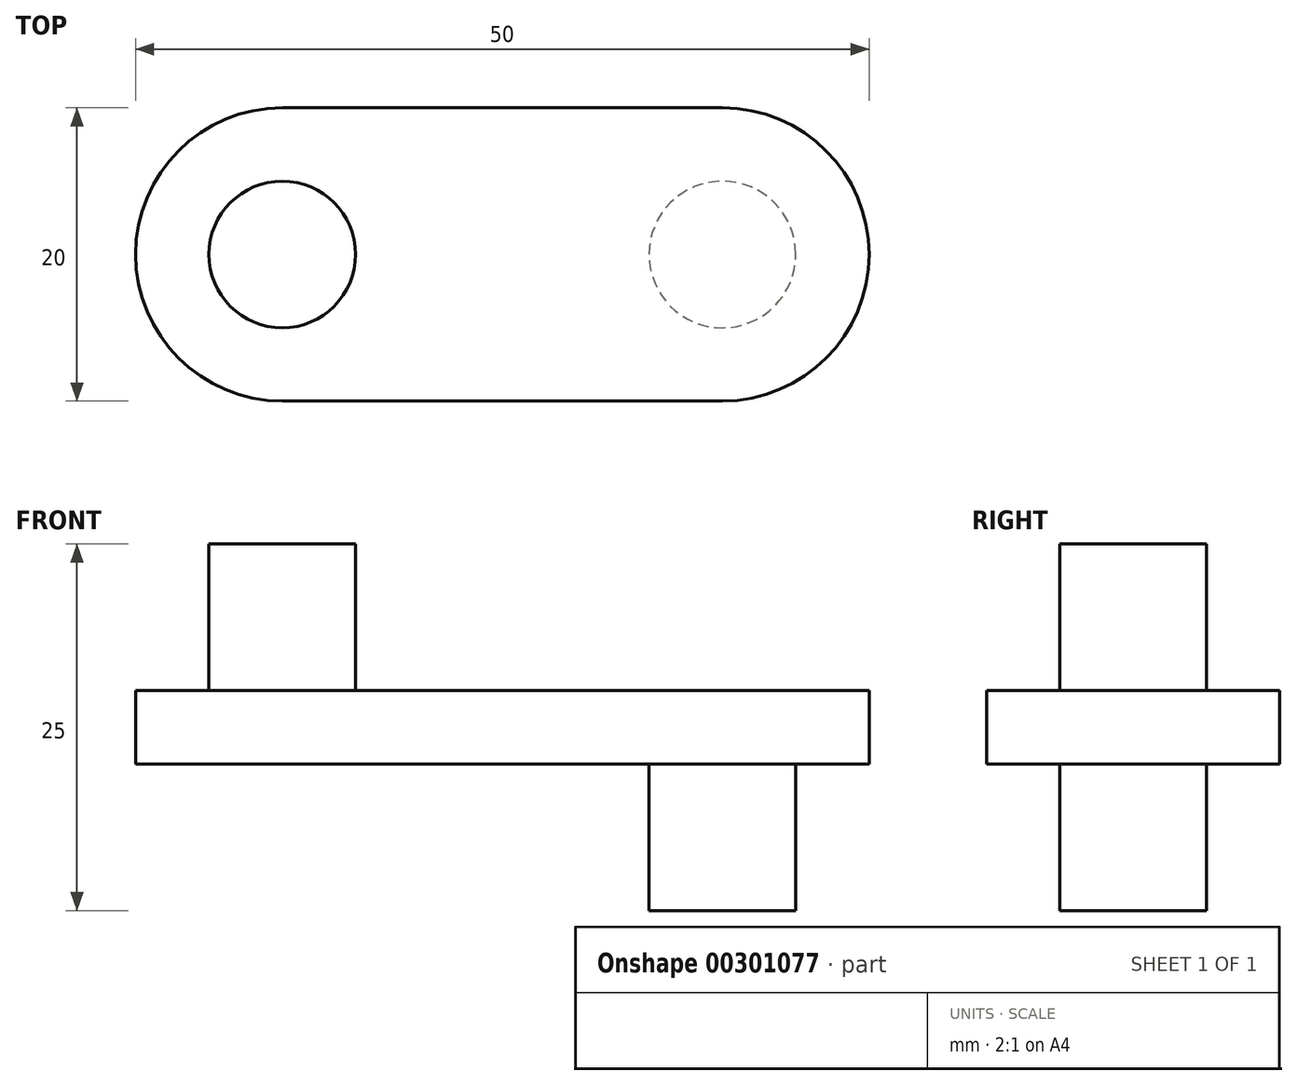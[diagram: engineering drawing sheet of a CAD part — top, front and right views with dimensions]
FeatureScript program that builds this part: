
annotation { "Feature Type Name" : "Feature", "Feature Type Description" : "" }
export const myFeature = defineFeature(function(context is Context, id is Id, definition is map)
    precondition{}
    {
        {
            var Q0;
            Q0=qCreatedBy(makeId("Top.planeOp"),FACE);
            var sketch = newSketch(context, id + "F0", { "sketchPlane" : qUnion([Q0])});
            skLineSegment(sketch, "E0", {"start": v(0, 0) * mm, "end": v(30, 0) * mm});
            skLineSegment(sketch, "E1", {"start": v(0, 20) * mm, "end": v(30, 20) * mm});
            skArc(sketch, "E2", {"start": v(0, 20) * mm, "mid": v(-10, 10) * mm, "end": v(0, 0) * mm});
            skArc(sketch, "E3", {"start": v(30, 0) * mm, "mid": v(40, 10) * mm, "end": v(30, 20) * mm});
            skSolve(sketch);
        }
        {
            var Q0;
            Q0 = qSketchRegion(id + "F0", true);
            extrude(context, id + "F1", {"entities" : qUnion([Q0]), "depth" : 5 * mm});
        }
        {
            var Q0;
            Q0=makeQuery(id+"F1.opExtrude","CAP_FACE",FACE,{"disambiguationData":[OSD([sQuery(id+"F0.wireOp",EDGE,"E0"),sQuery(id+"F0.wireOp",EDGE,"E1"),sQuery(id+"F0.wireOp",EDGE,"E2"),sQuery(id+"F0.wireOp",EDGE,"E3")])],"isStart":false});
            var sketch = newSketch(context, id + "F2", { "sketchPlane" : qUnion([Q0])});
            skCircle(sketch, "E4", {"center": v(0, 10) * mm, "radius": 5 * mm});
            skSolve(sketch);
        }
        {
            var Q0;
            Q0 = qSketchRegion(id + "F2", true);
            extrude(context, id + "F3", {"entities" : qUnion([Q0]), "operationType" : NewBodyOperationType.ADD, "depth" : 10 * mm});
        }
        {
            var Q0;
            Q0=makeQuery(id+"F1.opExtrude","CAP_FACE",FACE,{"disambiguationData":[OSD([sQuery(id+"F0.wireOp",EDGE,"E0"),sQuery(id+"F0.wireOp",EDGE,"E1"),sQuery(id+"F0.wireOp",EDGE,"E2"),sQuery(id+"F0.wireOp",EDGE,"E3")])],"isStart":true});
            var sketch = newSketch(context, id + "F4", { "sketchPlane" : qUnion([Q0])});
            skCircle(sketch, "E5", {"center": v(30, -10) * mm, "radius": 5 * mm});
            skSolve(sketch);
        }
        {
            var Q0;
            Q0 = qSketchRegion(id + "F4", true);
            extrude(context, id + "F5", {"entities" : qUnion([Q0]), "operationType" : NewBodyOperationType.ADD, "depth" : 10 * mm});
        }
    });
